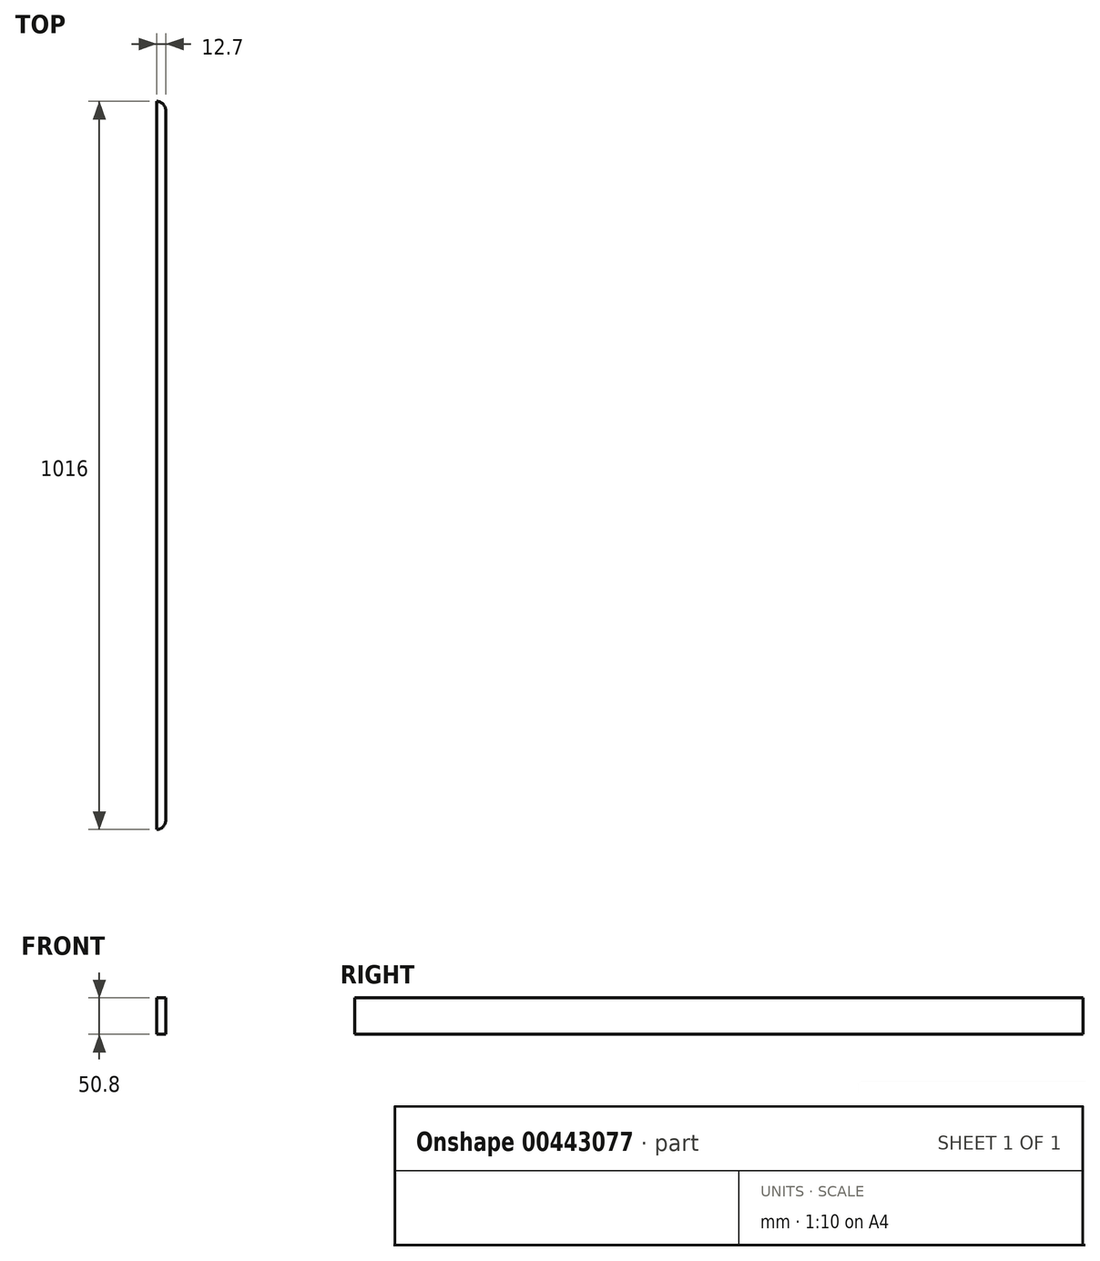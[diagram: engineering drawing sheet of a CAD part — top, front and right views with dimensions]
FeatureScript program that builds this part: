
annotation { "Feature Type Name" : "Feature", "Feature Type Description" : "" }
export const myFeature = defineFeature(function(context is Context, id is Id, definition is map)
    precondition{}
    {
        {
            var Q0;
            Q0=qCreatedBy(makeId("Front.planeOp"),FACE);
            var sketch = newSketch(context, id + "F0", { "sketchPlane" : qUnion([Q0])});
            skLineSegment(sketch, "E0.bottom", {"start": v(0, 0) * mm, "end": v(12.7, 0) * mm});
            skLineSegment(sketch, "E0.top", {"start": v(0, -50.8) * mm, "end": v(12.7, -50.8) * mm});
            skLineSegment(sketch, "E0.left", {"start": v(0, 0) * mm, "end": v(0, -50.8) * mm});
            skLineSegment(sketch, "E0.right", {"start": v(12.7, 0) * mm, "end": v(12.7, -50.8) * mm});
            skSolve(sketch);
        }
        {
            var Q0;
            Q0=makeQuery(id+"F0.imprint","IMPRINT",FACE,{"disambiguationData":[TD([[makeQuery(id+"F0.imprint","IMPRINT",EDGE,{"derivedFrom":sQuery(id+"F0.wireOp",EDGE,"E0.bottom")}),-1.0]])]});
            extrude(context, id + "F1", {"entities" : qUnion([Q0]), "endBound" : BoundingType.SYMMETRIC, "depth" : 1016 * mm});
        }
        {
            var Q0;
            Q0=makeQuery(id+"F1.opExtrude","CAP_EDGE",EDGE,{"disambiguationData":[OSD([sQuery(id+"F0.wireOp",EDGE,"E0.right")])],"isStart":false});
            var Q1;
            Q1=makeQuery(id+"F1.opExtrude","CAP_EDGE",EDGE,{"disambiguationData":[OSD([sQuery(id+"F0.wireOp",EDGE,"E0.right")])],"isStart":true});
            fillet(context, id + "F2", {"entities" : qUnion([Q0, Q1]), "radius" : 12.7 * mm, "tangentPropagation" : true, "allowEdgeOverflow" : false});
        }
    });
